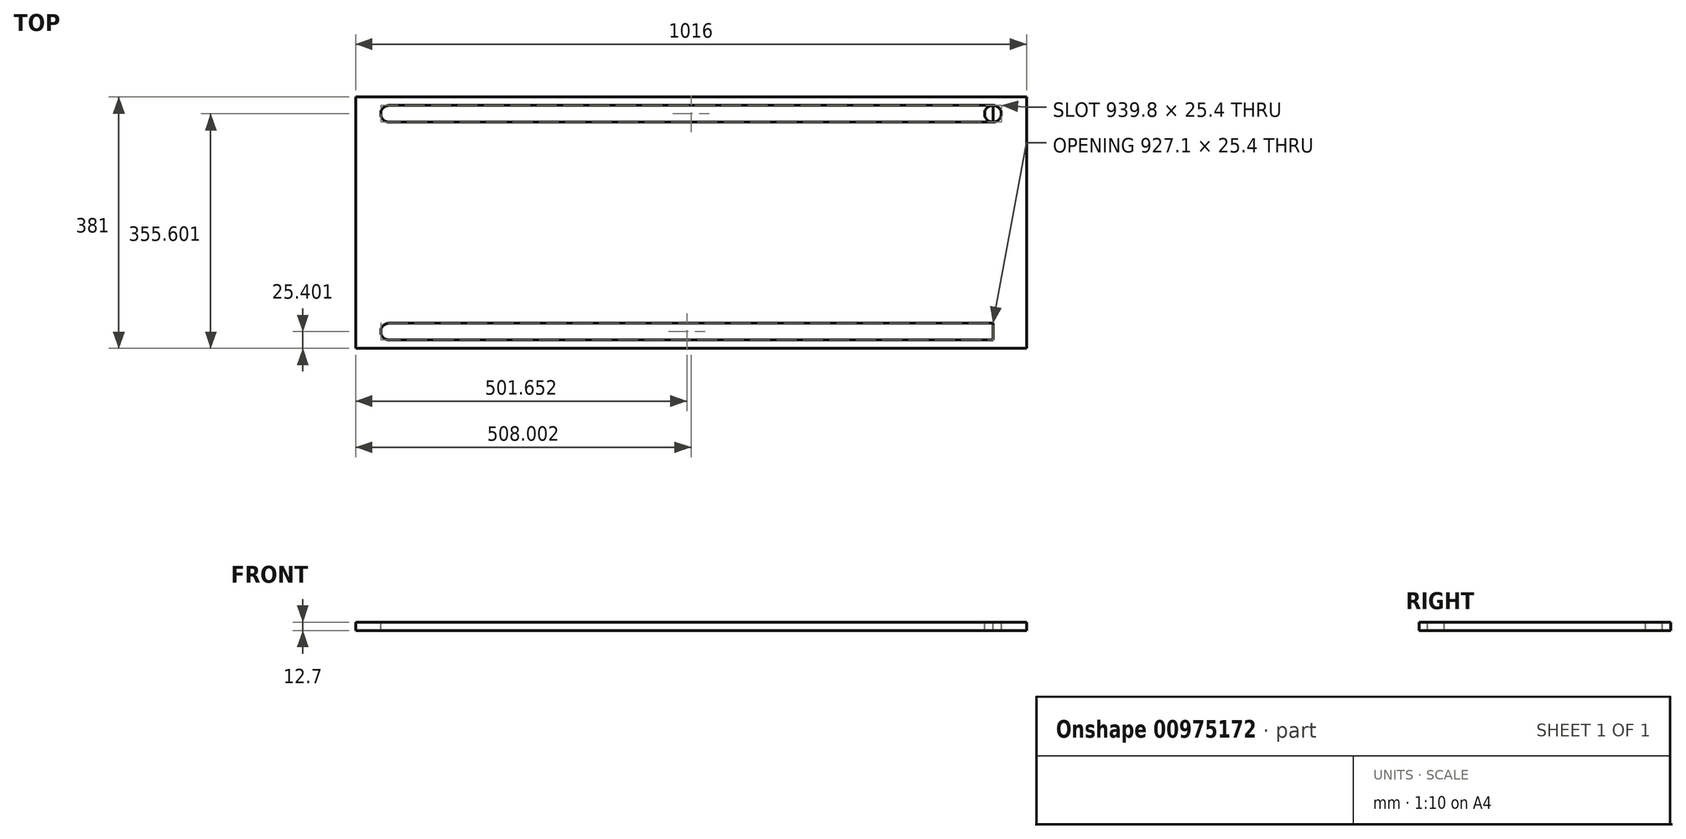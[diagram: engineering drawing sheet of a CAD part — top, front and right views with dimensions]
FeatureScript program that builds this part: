
annotation { "Feature Type Name" : "Feature", "Feature Type Description" : "" }
export const myFeature = defineFeature(function(context is Context, id is Id, definition is map)
    precondition{}
    {
        {
            var Q0;
            Q0=qCreatedBy(makeId("Top.planeOp"),FACE);
            var sketch = newSketch(context, id + "F0", { "sketchPlane" : qUnion([Q0])});
            skLineSegment(sketch, "E0.bottom", {"start": v(-960.78, 359.9) * mm, "end": v(55.22, 359.9) * mm});
            skLineSegment(sketch, "E0.top", {"start": v(-960.78, -21.1) * mm, "end": v(55.22, -21.1) * mm});
            skLineSegment(sketch, "E0.left", {"start": v(-960.78, 359.9) * mm, "end": v(-960.78, -21.1) * mm});
            skLineSegment(sketch, "E0.right", {"start": v(55.22, 359.9) * mm, "end": v(55.22, -21.1) * mm});
            skSolve(sketch);
        }
        {
            var Q0;
            Q0=makeQuery(id+"F0.imprint","IMPRINT",FACE,{"disambiguationData":[TD([[makeQuery(id+"F0.imprint","IMPRINT",EDGE,{"derivedFrom":sQuery(id+"F0.wireOp",EDGE,"E0.bottom")}),-1.0]])]});
            extrude(context, id + "F1", {"entities" : qUnion([Q0]), "depth" : 12.7 * mm, "offsetDistance" : 25.4 * mm});
        }
        {
            var Q0;
            Q0=makeQuery(id+"F1.opExtrude","CAP_FACE",FACE,{"disambiguationData":[OSD([sQuery(id+"F0.wireOp",EDGE,"E0.bottom"),sQuery(id+"F0.wireOp",EDGE,"E0.top"),sQuery(id+"F0.wireOp",EDGE,"E0.left"),sQuery(id+"F0.wireOp",EDGE,"E0.right")])],"isStart":false});
            var sketch = newSketch(context, id + "F2", { "sketchPlane" : qUnion([Q0])});
            skLineSegment(sketch, "E1.bottom", {"start": v(-960.78, 359.9) * mm, "end": v(-909.98, 359.9) * mm});
            skLineSegment(sketch, "E1.top", {"start": v(-960.78, -21.1) * mm, "end": v(-909.98, -21.1) * mm});
            skLineSegment(sketch, "E1.left", {"start": v(-960.78, 359.9) * mm, "end": v(-960.78, -21.1) * mm});
            skLineSegment(sketch, "E1.right", {"start": v(-909.98, 359.9) * mm, "end": v(-909.98, -21.1) * mm});
            skLineSegment(sketch, "E2.bottom", {"start": v(55.22, 359.9) * mm, "end": v(4.42, 359.9) * mm});
            skLineSegment(sketch, "E2.top", {"start": v(55.22, -21.1) * mm, "end": v(4.42, -21.1) * mm});
            skLineSegment(sketch, "E2.left", {"start": v(55.22, 359.9) * mm, "end": v(55.22, -21.1) * mm});
            skLineSegment(sketch, "E2.right", {"start": v(4.42, 359.9) * mm, "end": v(4.42, -21.1) * mm});
            skLineSegment(sketch, "E3.bottom", {"start": v(55.22, -21.1) * mm, "end": v(-960.78, -21.1) * mm});
            skLineSegment(sketch, "E3.top", {"start": v(55.22, 4.3) * mm, "end": v(-960.78, 4.3) * mm});
            skLineSegment(sketch, "E3.left", {"start": v(55.22, -21.1) * mm, "end": v(55.22, 4.3) * mm});
            skLineSegment(sketch, "E3.right", {"start": v(-960.78, -21.1) * mm, "end": v(-960.78, 4.3) * mm});
            skLineSegment(sketch, "E4.bottom", {"start": v(-960.78, 359.9) * mm, "end": v(55.22, 359.9) * mm});
            skLineSegment(sketch, "E4.top", {"start": v(-960.78, 334.5) * mm, "end": v(55.22, 334.5) * mm});
            skLineSegment(sketch, "E4.left", {"start": v(-960.78, 359.9) * mm, "end": v(-960.78, 334.5) * mm});
            skLineSegment(sketch, "E4.right", {"start": v(55.22, 359.9) * mm, "end": v(55.22, 334.5) * mm});
            skCircle(sketch, "E5", {"center": v(-909.98, 334.5) * mm, "radius": 12.7 * mm});
            skCircle(sketch, "E6", {"center": v(-909.98, 4.3) * mm, "radius": 12.7 * mm});
            skCircle(sketch, "E7", {"center": v(4.42, 334.5) * mm, "radius": 12.7 * mm});
            skCircle(sketch, "E8", {"center": v(4.42, 4.3) * mm, "radius": 12.7 * mm});
            skLineSegment(sketch, "E9.bottom", {"start": v(-8.28, 4.3) * mm, "end": v(17.12, 4.3) * mm});
            skLineSegment(sketch, "E9.top", {"start": v(-8.28, 334.5) * mm, "end": v(17.12, 334.5) * mm});
            skLineSegment(sketch, "E9.left", {"start": v(-8.28, 4.3) * mm, "end": v(-8.28, 334.5) * mm});
            skLineSegment(sketch, "E9.right", {"start": v(17.12, 4.3) * mm, "end": v(17.12, 334.5) * mm});
            skLineSegment(sketch, "E10.bottom", {"start": v(-909.98, 347.2) * mm, "end": v(4.42, 347.2) * mm});
            skLineSegment(sketch, "E10.top", {"start": v(-909.98, 321.8) * mm, "end": v(4.42, 321.8) * mm});
            skLineSegment(sketch, "E10.left", {"start": v(-909.98, 347.2) * mm, "end": v(-909.98, 321.8) * mm});
            skLineSegment(sketch, "E10.right", {"start": v(4.42, 347.2) * mm, "end": v(4.42, 321.8) * mm});
            skLineSegment(sketch, "E11.bottom", {"start": v(-909.98, -8.4) * mm, "end": v(4.42, -8.4) * mm});
            skLineSegment(sketch, "E11.top", {"start": v(-909.98, 17) * mm, "end": v(4.42, 17) * mm});
            skLineSegment(sketch, "E11.left", {"start": v(-909.98, -8.4) * mm, "end": v(-909.98, 17) * mm});
            skLineSegment(sketch, "E11.right", {"start": v(4.42, -8.4) * mm, "end": v(4.42, 17) * mm});
            skSolve(sketch);
        }
        {
            var Q0;
            {var subQ0=sQuery(id+"F2.wireOp",EDGE,"E10.left");var subQ1=sQuery(id+"F2.wireOp",EDGE,"E4.top");var subQ2=makeQuery(id+"F2.imprint","INTERSECT",VERTEX,{"derivedFrom":[subQ1,subQ0]});Q0=makeQuery(id+"F2.imprint","IMPRINT",FACE,{"disambiguationData":[TD([[makeQuery(id+"F2.imprint","IMPRINT",EDGE,{"disambiguationData":[TD([[subQ2,-1.0]])],"derivedFrom":subQ1}),-1.0]])]});}
            var Q1;
            {var subQ0=sQuery(id+"F2.wireOp",EDGE,"E10.left");var subQ1=sQuery(id+"F2.wireOp",EDGE,"E4.top");var subQ2=makeQuery(id+"F2.imprint","INTERSECT",VERTEX,{"derivedFrom":[subQ1,subQ0]});Q1=makeQuery(id+"F2.imprint","IMPRINT",FACE,{"disambiguationData":[TD([[makeQuery(id+"F2.imprint","IMPRINT",EDGE,{"disambiguationData":[TD([[subQ2,-1.0]])],"derivedFrom":subQ1}),1.0]])]});}
            var Q2;
            {var subQ0=sQuery(id+"F2.wireOp",EDGE,"E5");var subQ1=sQuery(id+"F2.wireOp",EDGE,"E4.top");var subQ2=makeQuery(id+"F2.imprint","INTERSECT",VERTEX,{"disambiguationData":[OD(0.0)],"derivedFrom":[subQ1,subQ0]});Q2=makeQuery(id+"F2.imprint","IMPRINT",FACE,{"disambiguationData":[TD([[makeQuery(id+"F2.imprint","IMPRINT",EDGE,{"disambiguationData":[TD([[subQ2,-1.0]])],"derivedFrom":subQ1}),1.0]])]});}
            var Q3;
            {var subQ0=sQuery(id+"F2.wireOp",EDGE,"E5");var subQ1=sQuery(id+"F2.wireOp",EDGE,"E4.top");var subQ2=makeQuery(id+"F2.imprint","INTERSECT",VERTEX,{"disambiguationData":[OD(0.0)],"derivedFrom":[subQ1,subQ0]});Q3=makeQuery(id+"F2.imprint","IMPRINT",FACE,{"disambiguationData":[TD([[makeQuery(id+"F2.imprint","IMPRINT",EDGE,{"disambiguationData":[TD([[subQ2,-1.0]])],"derivedFrom":subQ1}),-1.0]])]});}
            var Q4;
            {var subQ1=sQuery(id+"F2.wireOp",EDGE,"E4.top");var subQ3=sQuery(id+"F2.wireOp",EDGE,"E5");var subQ4=makeQuery(id+"F2.imprint","INTERSECT",VERTEX,{"disambiguationData":[OD(1.0)],"derivedFrom":[subQ1,subQ3]});Q4=makeQuery(id+"F2.imprint","IMPRINT",FACE,{"disambiguationData":[TD([[makeQuery(id+"F2.imprint","IMPRINT",EDGE,{"disambiguationData":[TD([[subQ4,-1.0]])],"derivedFrom":subQ1}),-1.0]])]});}
            var Q5;
            {var subQ5=sQuery(id+"F2.wireOp",EDGE,"E10.bottom");Q5=makeQuery(id+"F2.imprint","IMPRINT",FACE,{"disambiguationData":[TD([[makeQuery(id+"F2.imprint","IMPRINT",EDGE,{"derivedFrom":subQ5}),-1.0]])]});}
            var Q6;
            {var subQ0=sQuery(id+"F2.wireOp",EDGE,"E6");var subQ1=sQuery(id+"F2.wireOp",EDGE,"E3.top");var subQ2=makeQuery(id+"F2.imprint","INTERSECT",VERTEX,{"disambiguationData":[OD(0.0)],"derivedFrom":[subQ1,subQ0]});Q6=makeQuery(id+"F2.imprint","IMPRINT",FACE,{"disambiguationData":[TD([[makeQuery(id+"F2.imprint","IMPRINT",EDGE,{"disambiguationData":[TD([[subQ2,-1.0]])],"derivedFrom":subQ1}),-1.0]])]});}
            var Q7;
            {var subQ0=sQuery(id+"F2.wireOp",EDGE,"E11.left");var subQ1=sQuery(id+"F2.wireOp",EDGE,"E3.top");var subQ2=makeQuery(id+"F2.imprint","INTERSECT",VERTEX,{"derivedFrom":[subQ1,subQ0]});Q7=makeQuery(id+"F2.imprint","IMPRINT",FACE,{"disambiguationData":[TD([[makeQuery(id+"F2.imprint","IMPRINT",EDGE,{"disambiguationData":[TD([[subQ2,-1.0]])],"derivedFrom":subQ1}),-1.0]])]});}
            var Q8;
            {var subQ0=sQuery(id+"F2.wireOp",EDGE,"E11.left");var subQ1=sQuery(id+"F2.wireOp",EDGE,"E3.top");var subQ2=makeQuery(id+"F2.imprint","INTERSECT",VERTEX,{"derivedFrom":[subQ1,subQ0]});Q8=makeQuery(id+"F2.imprint","IMPRINT",FACE,{"disambiguationData":[TD([[makeQuery(id+"F2.imprint","IMPRINT",EDGE,{"disambiguationData":[TD([[subQ2,-1.0]])],"derivedFrom":subQ1}),1.0]])]});}
            var Q9;
            {var subQ0=sQuery(id+"F2.wireOp",EDGE,"E6");var subQ1=sQuery(id+"F2.wireOp",EDGE,"E3.top");var subQ2=makeQuery(id+"F2.imprint","INTERSECT",VERTEX,{"disambiguationData":[OD(0.0)],"derivedFrom":[subQ1,subQ0]});Q9=makeQuery(id+"F2.imprint","IMPRINT",FACE,{"disambiguationData":[TD([[makeQuery(id+"F2.imprint","IMPRINT",EDGE,{"disambiguationData":[TD([[subQ2,-1.0]])],"derivedFrom":subQ1}),1.0]])]});}
            var Q10;
            {var subQ1=sQuery(id+"F2.wireOp",EDGE,"E3.top");var subQ3=sQuery(id+"F2.wireOp",EDGE,"E6");var subQ4=makeQuery(id+"F2.imprint","INTERSECT",VERTEX,{"disambiguationData":[OD(0.0)],"derivedFrom":[subQ1,subQ3]});Q10=makeQuery(id+"F2.imprint","IMPRINT",FACE,{"disambiguationData":[TD([[makeQuery(id+"F2.imprint","IMPRINT",EDGE,{"disambiguationData":[TD([[subQ4,1.0]])],"derivedFrom":subQ1}),-1.0]])]});}
            var Q11;
            {var subQ5=sQuery(id+"F2.wireOp",EDGE,"E11.bottom");Q11=makeQuery(id+"F2.imprint","IMPRINT",FACE,{"disambiguationData":[TD([[makeQuery(id+"F2.imprint","IMPRINT",EDGE,{"derivedFrom":subQ5}),1.0]])]});}
            var Q12;
            {var subQ0=sQuery(id+"F2.wireOp",EDGE,"E9.left");var subQ3=sQuery(id+"F2.wireOp",EDGE,"E11.top");var subQ5=makeQuery(id+"F2.imprint","INTERSECT",VERTEX,{"derivedFrom":[subQ0,subQ3]});Q12=makeQuery(id+"F2.imprint","IMPRINT",FACE,{"disambiguationData":[TD([[makeQuery(id+"F2.imprint","IMPRINT",EDGE,{"disambiguationData":[TD([[subQ5,1.0]])],"derivedFrom":subQ0}),-1.0]])]});}
            var Q13;
            {var subQ0=sQuery(id+"F2.wireOp",EDGE,"E9.bottom");var subQ3=sQuery(id+"F2.wireOp",EDGE,"E11.right");var subQ5=makeQuery(id+"F2.imprint","INTERSECT",VERTEX,{"derivedFrom":[subQ0,subQ3]});Q13=makeQuery(id+"F2.imprint","IMPRINT",FACE,{"disambiguationData":[TD([[makeQuery(id+"F2.imprint","IMPRINT",EDGE,{"disambiguationData":[TD([[subQ5,1.0]])],"derivedFrom":subQ0}),1.0]])]});}
            var Q14;
            {var subQ0=sQuery(id+"F2.wireOp",EDGE,"E9.bottom");var subQ3=sQuery(id+"F2.wireOp",EDGE,"E11.right");var subQ5=makeQuery(id+"F2.imprint","INTERSECT",VERTEX,{"derivedFrom":[subQ0,subQ3]});Q14=makeQuery(id+"F2.imprint","IMPRINT",FACE,{"disambiguationData":[TD([[makeQuery(id+"F2.imprint","IMPRINT",EDGE,{"disambiguationData":[TD([[subQ5,-1.0]])],"derivedFrom":subQ0}),1.0]])]});}
            var Q15;
            {var subQ0=sQuery(id+"F2.wireOp",EDGE,"E9.bottom");var subQ3=sQuery(id+"F2.wireOp",EDGE,"E11.right");var subQ5=makeQuery(id+"F2.imprint","INTERSECT",VERTEX,{"derivedFrom":[subQ0,subQ3]});Q15=makeQuery(id+"F2.imprint","IMPRINT",FACE,{"disambiguationData":[TD([[makeQuery(id+"F2.imprint","IMPRINT",EDGE,{"disambiguationData":[TD([[subQ5,-1.0]])],"derivedFrom":subQ0}),-1.0]])]});}
            var Q16;
            {var subQ0=sQuery(id+"F2.wireOp",EDGE,"E9.bottom");var subQ3=sQuery(id+"F2.wireOp",EDGE,"E11.right");var subQ5=makeQuery(id+"F2.imprint","INTERSECT",VERTEX,{"derivedFrom":[subQ0,subQ3]});Q16=makeQuery(id+"F2.imprint","IMPRINT",FACE,{"disambiguationData":[TD([[makeQuery(id+"F2.imprint","IMPRINT",EDGE,{"disambiguationData":[TD([[subQ5,1.0]])],"derivedFrom":subQ0}),-1.0]])]});}
            var Q17;
            {var subQ0=sQuery(id+"F2.wireOp",EDGE,"E9.left");var subQ3=sQuery(id+"F2.wireOp",EDGE,"E10.top");var subQ5=makeQuery(id+"F2.imprint","INTERSECT",VERTEX,{"derivedFrom":[subQ0,subQ3]});Q17=makeQuery(id+"F2.imprint","IMPRINT",FACE,{"disambiguationData":[TD([[makeQuery(id+"F2.imprint","IMPRINT",EDGE,{"disambiguationData":[TD([[subQ5,-1.0]])],"derivedFrom":subQ0}),-1.0]])]});}
            var Q18;
            {var subQ0=sQuery(id+"F2.wireOp",EDGE,"E9.top");var subQ3=sQuery(id+"F2.wireOp",EDGE,"E10.right");var subQ5=makeQuery(id+"F2.imprint","INTERSECT",VERTEX,{"derivedFrom":[subQ0,subQ3]});Q18=makeQuery(id+"F2.imprint","IMPRINT",FACE,{"disambiguationData":[TD([[makeQuery(id+"F2.imprint","IMPRINT",EDGE,{"disambiguationData":[TD([[subQ5,1.0]])],"derivedFrom":subQ0}),-1.0]])]});}
            var Q19;
            {var subQ0=sQuery(id+"F2.wireOp",EDGE,"E9.top");var subQ3=sQuery(id+"F2.wireOp",EDGE,"E10.right");var subQ5=makeQuery(id+"F2.imprint","INTERSECT",VERTEX,{"derivedFrom":[subQ0,subQ3]});Q19=makeQuery(id+"F2.imprint","IMPRINT",FACE,{"disambiguationData":[TD([[makeQuery(id+"F2.imprint","IMPRINT",EDGE,{"disambiguationData":[TD([[subQ5,1.0]])],"derivedFrom":subQ0}),1.0]])]});}
            var Q20;
            {var subQ0=sQuery(id+"F2.wireOp",EDGE,"E9.top");var subQ3=sQuery(id+"F2.wireOp",EDGE,"E10.right");var subQ5=makeQuery(id+"F2.imprint","INTERSECT",VERTEX,{"derivedFrom":[subQ0,subQ3]});Q20=makeQuery(id+"F2.imprint","IMPRINT",FACE,{"disambiguationData":[TD([[makeQuery(id+"F2.imprint","IMPRINT",EDGE,{"disambiguationData":[TD([[subQ5,-1.0]])],"derivedFrom":subQ0}),1.0]])]});}
            var Q21;
            {var subQ0=sQuery(id+"F2.wireOp",EDGE,"E9.top");var subQ3=sQuery(id+"F2.wireOp",EDGE,"E10.right");var subQ5=makeQuery(id+"F2.imprint","INTERSECT",VERTEX,{"derivedFrom":[subQ0,subQ3]});Q21=makeQuery(id+"F2.imprint","IMPRINT",FACE,{"disambiguationData":[TD([[makeQuery(id+"F2.imprint","IMPRINT",EDGE,{"disambiguationData":[TD([[subQ5,-1.0]])],"derivedFrom":subQ0}),-1.0]])]});}
            extrude(context, id + "F3", {"entities" : qUnion([Q0, Q1, Q2, Q3, Q4, Q5, Q6, Q7, Q8, Q9, Q10, Q11, Q12, Q13, Q14, Q15, Q16, Q17, Q18, Q19, Q20, Q21]), "operationType" : NewBodyOperationType.REMOVE, "oppositeDirection" : true, "depth" : 25.4 * mm, "offsetDistance" : 25.4 * mm});
        }
    });
